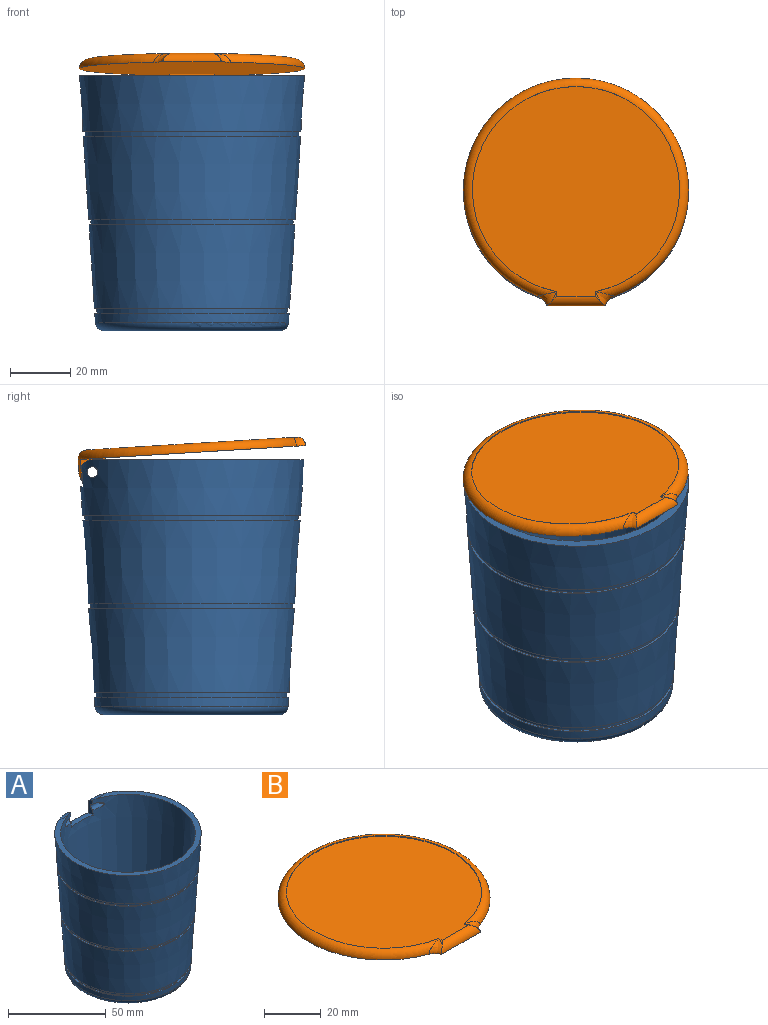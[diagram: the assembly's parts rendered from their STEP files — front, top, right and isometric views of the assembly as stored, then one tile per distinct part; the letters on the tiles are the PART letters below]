
ASSEMBLY  parts=2 mates=1
PART A: 27 faces, bbox 75x75x85 mm
  f0: plane 75x70.5mm, normal (0,0,1), area 591.8mm2, adj f1,f2,f24,f26
  f1: cone r=34.49mm half-angle=3.7deg, axis (0,0,1), area 15739.4mm2, adj f0,f17,f20,f21,f22,f23,f24,f25
  f2: cone r=32mm half-angle=3.7deg, axis (0,0,1), area 4120.8mm2, adj f0,f5,f20,f21,f22,f23,f24,f25
  f3: plane 52.75x52.75mm, normal (0,0,1), area 2185.5mm2, adj f17
  f4: cone r=36.89mm half-angle=86.3deg, axis (0,0,-1), area 157.6mm2, adj f6,f7
  f5: cone r=35.6mm half-angle=86.3deg, axis (0,0,-1), area 158.1mm2, adj f2,f6
  f6: cone r=35.49mm half-angle=3.7deg, axis (0,0,1), area 357.3mm2, adj f4,f5
  f7: cone r=32mm half-angle=3.7deg, axis (0,0,1), area 6193.7mm2, adj f4,f9
  f8: cone r=34.98mm half-angle=86.3deg, axis (0,0,-1), area 149.3mm2, adj f10,f11
  f9: cone r=33.69mm half-angle=86.3deg, axis (0,0,-1), area 149.7mm2, adj f7,f10
  f10: cone r=33.59mm half-angle=3.7deg, axis (0,0,1), area 338.2mm2, adj f8,f9
  f11: cone r=32mm half-angle=3.7deg, axis (0,0,1), area 5859mm2, adj f8,f13
  f12: cone r=33.08mm half-angle=86.3deg, axis (0,0,-1), area 140.9mm2, adj f14,f15
  f13: cone r=31.78mm half-angle=86.3deg, axis (0,0,-1), area 141.3mm2, adj f11,f14
  f14: cone r=31.68mm half-angle=3.7deg, axis (0,0,1), area 319mm2, adj f12,f13
  f15: cone r=32mm half-angle=3.7deg, axis (0,0,1), area 619.6mm2, adj f12,f16
  f16: torus R=29.19mm, axis (0,0,1), area 881.6mm2, adj f15,f18
  f17: torus R=26.38mm, axis (0,0,-1), area 801.7mm2, adj f1,f3
  f18: cylinder r=29.19mm len=58.38mm, axis (0,0,-1), area 55mm2, adj f16,f19
  f19: plane 58.38x58.38mm, normal (0,0,-1), area 2676.4mm2, adj f18
  f20: plane 15.6x3.92mm, normal (0,0,1), area 47.3mm2, adj f1,f2,f21,f22
  f21: plane 8.96x3.55mm, normal (-1,0,0), area 21.6mm2, adj f1,f2,f20,f25,f26
  f22: plane 8.96x3.55mm, normal (1,0,0), area 21.6mm2, adj f1,f2,f20,f23,f24
  f23: cylinder r=1.8mm len=12.52mm, axis (1,0,0), area 77.6mm2, adj f1,f2,f22
  f24: cylinder r=4.2mm len=10.01mm, axis (1,0,0), area 21.9mm2, adj f0,f1,f2,f22
  f25: cylinder r=1.8mm len=12.52mm, axis (1,0,0), area 77.5mm2, adj f1,f2,f21
  f26: cylinder r=4.2mm len=10.01mm, axis (1,0,0), area 21.9mm2, adj f0,f1,f2,f21
PART B: 18 faces, bbox 81.3x80.7x12.1 mm
  f0: plane 9x8.24mm, normal (-1,0,0), area 57.4mm2, adj f2,f3,f10,f11,f12
  f1: plane 9x8.24mm, normal (1,0,0), area 57.4mm2, adj f2,f3,f10,f11,f12
  f2: cylinder r=37.5mm len=15mm, axis (0,0,1), area 86.8mm2, adj f0,f1,f4,f12
  f3: plane 75.34x75.1mm, normal (0,0,-1), area 4317.8mm2, adj f0,f1,f4,f7,f8,f9,f10
  f4: torus R=34.5mm, axis (0,0,1), area 985.9mm2, adj f2,f3,f8,f9,f16
  f5: cylinder r=3mm len=3.05mm, axis (0,1,0), area 1.2mm2, adj f7,f8,f13
  f6: cylinder r=3mm len=3.05mm, axis (0,-1,0), area 1.2mm2, adj f7,f9,f15
  f7: cylinder r=3mm len=19.34mm, axis (-1,0,0), area 77.9mm2, adj f3,f5,f6,f8,f9,f14
  f8: bspline ~6.31x6.08mm, area 14.3mm2, adj f3,f4,f5,f7
  f9: bspline ~6.31x6.08mm, area 14.3mm2, adj f3,f4,f6,f7
  f10: plane 15x4.5mm, normal (0,-1,0), area 67.5mm2, adj f0,f1,f3,f12
  f11: cylinder r=1.8mm len=15mm, axis (-1,0,0), area 169.6mm2, adj f0,f1
  f12: cylinder r=4.5mm len=15mm, axis (-1,0,0), area 192.2mm2, adj f0,f1,f2,f10
  f13: plane 1.61x0.3mm, normal (1,0,0), area 0.5mm2, adj f5,f14,f16,f17
  f14: plane 12.9x0.3mm, normal (0,1,0), area 3.9mm2, adj f7,f13,f15,f17
  f15: plane 1.61x0.3mm, normal (-1,0,0), area 0.5mm2, adj f6,f14,f16,f17
  f16: cylinder r=34.5mm len=69mm, axis (0,0,1), area 61.1mm2, adj f4,f13,f15,f17
  f17: plane 70x69mm, normal (0,0,1), area 3754.8mm2, adj f13,f14,f15,f16
PLACE A t=(4.45,5.77,-14.09)mm fixed
PLACE B rot(axis=(-1,0,0),3.5deg) t=(4.45,0.9,-11.93)mm
MATE revolute B.f11 <-> A.f23  axis (-1,0,0) through (-3.05,38.77,66.71)mm
